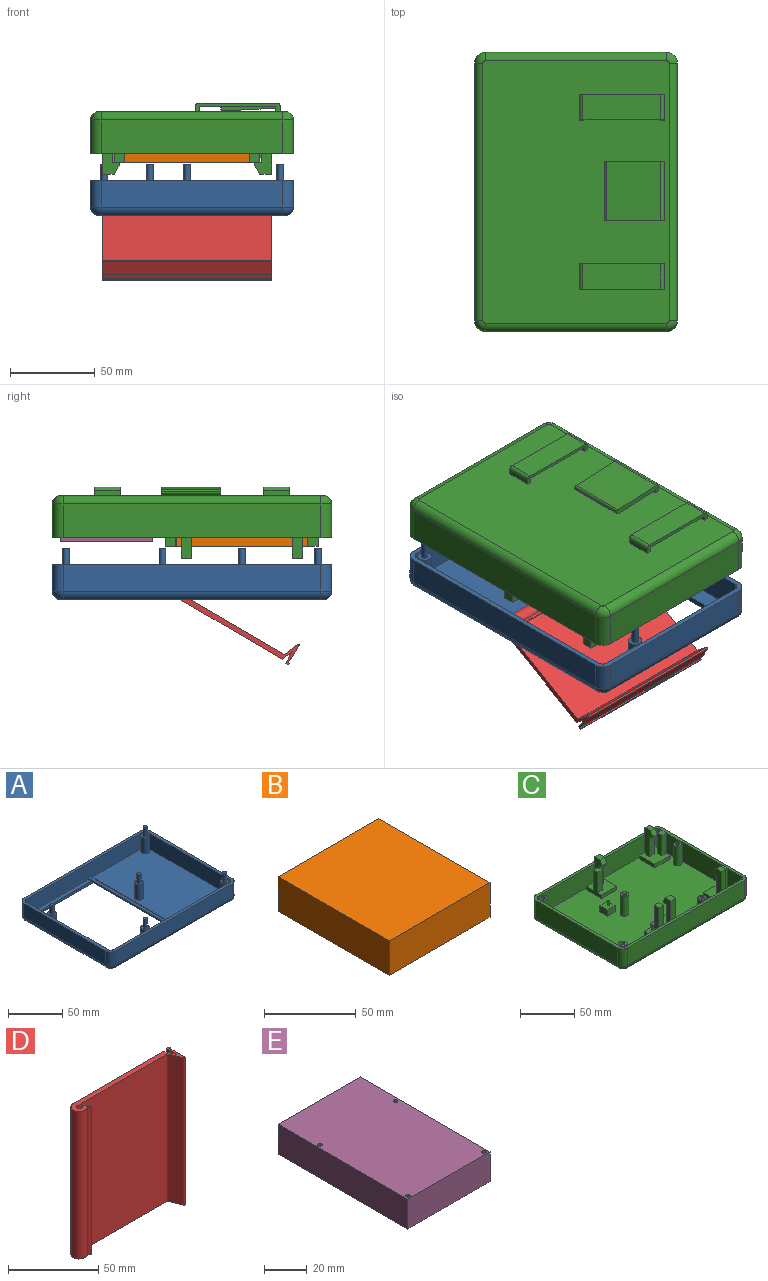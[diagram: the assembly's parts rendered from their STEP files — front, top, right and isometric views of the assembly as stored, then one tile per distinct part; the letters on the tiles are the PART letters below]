
ASSEMBLY  parts=5 mates=8
PART A: 52 faces, bbox 165x120x30.5 mm
  f0: plane 154.84x109.84mm, normal (0,0,-1), area 9006.2mm2, adj f19,f20,f21,f22,f23,f24,f25,f26
  f1: plane 159x114mm, normal (0,0,1), area 9865mm2, adj f11,f12,f13,f14,f15,f16,f17,f18
  f2: plane 107.3x15.92mm, normal (1,0,0), area 1708.2mm2, adj f3,f9,f10,f25
  f3: cylinder r=6.35mm len=15.92mm, axis (0,0,-1), area 158.8mm2, adj f2,f4,f10,f23
  f4: plane 152.3x15.92mm, normal (0,1,0), area 2424.6mm2, adj f3,f5,f10,f21
  f5: cylinder r=6.35mm len=15.92mm, axis (0,0,-1), area 158.8mm2, adj f4,f6,f10,f19
  f6: plane 107.3x15.92mm, normal (-1,0,0), area 1708.2mm2, adj f5,f7,f10,f20
  f7: cylinder r=6.35mm len=15.92mm, axis (0,0,-1), area 158.8mm2, adj f6,f8,f10,f22
  f8: plane 152.3x15.92mm, normal (0,-1,0), area 2424.6mm2, adj f7,f9,f10,f24
  f9: cylinder r=6.35mm len=15.92mm, axis (0,0,-1), area 158.8mm2, adj f2,f8,f10,f26
  f10: plane 165x120mm, normal (0,0,1), area 1649mm2, adj f2,f3,f4,f5,f6,f7,f8,f9
  f11: plane 107.3x18mm, normal (-1,0,0), area 1931.4mm2, adj f1,f10,f12,f18
  f12: cylinder r=3.35mm len=18mm, axis (0,0,-1), area 94.7mm2, adj f1,f10,f11,f13
  f13: plane 152.3x18mm, normal (0,-1,0), area 2734.3mm2, adj f1,f10,f12,f14,f51
  f14: cylinder r=3.35mm len=18mm, axis (0,0,-1), area 94.7mm2, adj f1,f10,f13,f15
  f15: plane 107.3x18mm, normal (1,0,0), area 1931.4mm2, adj f1,f10,f14,f16
  f16: cylinder r=3.35mm len=18mm, axis (0,0,-1), area 94.7mm2, adj f1,f10,f15,f17
  f17: plane 152.3x18mm, normal (0,1,0), area 2734.3mm2, adj f1,f10,f16,f18,f51
  f18: cylinder r=3.35mm len=18mm, axis (0,0,-1), area 94.7mm2, adj f1,f10,f11,f17
  f19: torus R=1.27mm, axis (0,0,1), area 56.5mm2, adj f0,f5,f20,f21
  f20: cylinder r=5.08mm len=107.3mm, axis (0,-1,0), area 856.2mm2, adj f0,f6,f19,f22
  f21: cylinder r=5.08mm len=152.3mm, axis (-1,0,0), area 1215.3mm2, adj f0,f4,f19,f23
  f22: torus R=1.27mm, axis (0,0,1), area 56.5mm2, adj f0,f7,f20,f24
  f23: torus R=1.27mm, axis (0,0,1), area 56.5mm2, adj f0,f3,f21,f25
  f24: cylinder r=5.08mm len=152.3mm, axis (1,0,0), area 1215.3mm2, adj f0,f8,f22,f26
  f25: cylinder r=5.08mm len=107.3mm, axis (0,1,0), area 856.2mm2, adj f0,f2,f23,f26
  f26: torus R=1.27mm, axis (0,0,1), area 56.5mm2, adj f0,f9,f24,f25
  f27: cylinder r=4mm len=17.5mm, axis (0,0,-1), area 439.8mm2, adj f1,f28
  f28: plane 8x8mm, normal (0,0,1), area 38.3mm2, adj f27,f37
  f29: cylinder r=4mm len=17.5mm, axis (0,0,-1), area 439.8mm2, adj f1,f30
  f30: plane 8x8mm, normal (0,0,1), area 38.3mm2, adj f29,f41
  f31: cylinder r=4mm len=17.5mm, axis (0,0,-1), area 439.8mm2, adj f1,f32
  f32: plane 8x8mm, normal (0,0,1), area 38.3mm2, adj f31,f39
  f33: cylinder r=4mm len=17.5mm, axis (0,0,-1), area 439.8mm2, adj f1,f34
  f34: plane 8x8mm, normal (0,0,1), area 38.3mm2, adj f33,f45
  f35: cylinder r=4mm len=17.5mm, axis (0,0,-1), area 439.8mm2, adj f1,f36
  f36: plane 8x8mm, normal (0,0,1), area 38.3mm2, adj f35,f43
  f37: cylinder r=1.95mm len=10mm, axis (0,0,-1), area 122.5mm2, adj f28,f38
  f38: plane 3.9x3.9mm, normal (0,0,1), area 11.9mm2, adj f37
  f39: cylinder r=1.95mm len=10mm, axis (0,0,-1), area 122.5mm2, adj f32,f40
  f40: plane 3.9x3.9mm, normal (0,0,1), area 11.9mm2, adj f39
  f41: cylinder r=1.95mm len=10mm, axis (0,0,-1), area 122.5mm2, adj f30,f42
  f42: plane 3.9x3.9mm, normal (0,0,1), area 11.9mm2, adj f41
  f43: cylinder r=1.95mm len=10mm, axis (0,0,-1), area 122.5mm2, adj f36,f44
  f44: plane 3.9x3.9mm, normal (0,0,1), area 11.9mm2, adj f43
  f45: cylinder r=1.95mm len=10mm, axis (0,0,-1), area 122.5mm2, adj f34,f46
  f46: plane 3.9x3.9mm, normal (0,0,1), area 11.9mm2, adj f45
  f47: plane 80x3mm, normal (0,1,0), area 240mm2, adj f0,f1,f48,f50
  f48: plane 100x3mm, normal (1,0,0), area 300mm2, adj f0,f1,f47,f49
  f49: plane 80x3mm, normal (0,-1,0), area 240mm2, adj f0,f1,f48,f50
  f50: plane 100x3mm, normal (-1,0,0), area 300mm2, adj f0,f1,f47,f49
  f51: cylinder r=1.5mm len=114mm, axis (0,1,0), area 1074.4mm2, adj f13,f17
PART B: 6 faces, bbox 77.6x85.4x23 mm
  f0: plane 85.4x23mm, normal (-1,0,0), area 1964.2mm2, adj f1,f3,f4,f5
  f1: plane 77.6x23mm, normal (0,-1,0), area 1784.8mm2, adj f0,f2,f4,f5
  f2: plane 85.4x23mm, normal (1,0,0), area 1964.2mm2, adj f1,f3,f4,f5
  f3: plane 77.6x23mm, normal (0,1,0), area 1784.8mm2, adj f0,f2,f4,f5
  f4: plane 85.4x77.6mm, normal (0,0,1), area 6627mm2, adj f0,f1,f2,f3
  f5: plane 85.4x77.6mm, normal (0,0,-1), area 6627mm2, adj f0,f1,f2,f3
PART C: 177 faces, bbox 165x120x42 mm
  f0: plane 155x110mm, normal (0,0,-1), area 16793.4mm2, adj f139,f140,f141,f142,f143,f144,f145,f146
  f1: plane 159x114mm, normal (0,0,1), area 15865mm2, adj f17,f18,f19,f20,f21,f22,f23,f24
  f2: plane 20x20mm, normal (0,0,1), area 340mm2, adj f33,f34,f35,f36,f52,f53,f54,f82
  f3: plane 6x4mm, normal (0,0,-1), area 24mm2, adj f74,f79,f80,f81
  f4: plane 6x4mm, normal (0,0,-1), area 24mm2, adj f66,f71,f72,f73
  f5: plane 20x20mm, normal (0,0,1), area 340mm2, adj f37,f38,f39,f40,f48,f49,f50,f66
  f6: plane 20x20mm, normal (0,0,1), area 340mm2, adj f29,f30,f31,f32,f45,f46,f47,f56
  f7: plane 20x20mm, normal (0,0,1), area 340mm2, adj f25,f26,f27,f28,f41,f42,f43,f74
  f8: plane 165x120mm, normal (0,0,1), area 1649mm2, adj f9,f10,f11,f12,f13,f14,f15,f16
  f9: plane 107.3x20mm, normal (-1,0,0), area 2146mm2, adj f8,f10,f16,f142
  f10: cylinder r=6.35mm len=20mm, axis (0,0,-1), area 199.5mm2, adj f8,f9,f11,f140
  f11: plane 152.3x20mm, normal (0,-1,0), area 3046mm2, adj f8,f10,f12,f139
  f12: cylinder r=6.35mm len=20mm, axis (0,0,-1), area 199.5mm2, adj f8,f11,f13,f141
  f13: plane 107.3x20mm, normal (1,0,0), area 2146mm2, adj f8,f12,f14,f143
  f14: cylinder r=6.35mm len=20mm, axis (0,0,-1), area 199.5mm2, adj f8,f13,f15,f145
  f15: plane 152.3x20mm, normal (0,1,0), area 3046mm2, adj f8,f14,f16,f146
  f16: cylinder r=6.35mm len=20mm, axis (0,0,-1), area 199.5mm2, adj f8,f9,f15,f144
  f17: plane 107.3x22mm, normal (1,0,0), area 2360.6mm2, adj f1,f8,f18,f24
  f18: cylinder r=3.35mm len=22mm, axis (0,0,-1), area 115.8mm2, adj f1,f8,f17,f19
  f19: plane 152.3x22mm, normal (0,1,0), area 3350.6mm2, adj f1,f8,f18,f20
  f20: cylinder r=3.35mm len=22mm, axis (0,0,-1), area 115.8mm2, adj f1,f8,f19,f21
  f21: plane 107.3x22mm, normal (-1,0,0), area 2360.6mm2, adj f1,f8,f20,f22
  f22: cylinder r=3.35mm len=22mm, axis (0,0,-1), area 115.8mm2, adj f1,f8,f21,f23
  f23: plane 152.3x22mm, normal (0,-1,0), area 3350.6mm2, adj f1,f8,f22,f24
  f24: cylinder r=3.35mm len=22mm, axis (0,0,-1), area 115.8mm2, adj f1,f8,f17,f23
  f25: plane 27x20mm, normal (1,0,0), area 218mm2, adj f1,f7,f26,f28,f41,f43,f44
  f26: plane 20x4mm, normal (0,1,0), area 80mm2, adj f1,f7,f25,f27
  f27: plane 20x4mm, normal (-1,0,0), area 80mm2, adj f1,f7,f26,f28
  f28: plane 20x4mm, normal (0,-1,0), area 80mm2, adj f1,f7,f25,f27
  f29: plane 20x4mm, normal (0,-1,0), area 80mm2, adj f1,f6,f30,f32
  f30: plane 20x4mm, normal (1,0,0), area 80mm2, adj f1,f6,f29,f31
  f31: plane 20x4mm, normal (0,1,0), area 80mm2, adj f1,f6,f30,f32
  f32: plane 27x20mm, normal (-1,0,0), area 218mm2, adj f1,f6,f29,f31,f45,f47,f65
  f33: plane 20x4mm, normal (0,-1,0), area 80mm2, adj f1,f2,f34,f36
  f34: plane 27x20mm, normal (1,0,0), area 218mm2, adj f1,f2,f33,f35,f52,f54,f55
  f35: plane 20x4mm, normal (0,1,0), area 80mm2, adj f1,f2,f34,f36
  f36: plane 20x4mm, normal (-1,0,0), area 80mm2, adj f1,f2,f33,f35
  f37: plane 27x20mm, normal (-1,0,0), area 218mm2, adj f1,f5,f38,f40,f48,f50,f51
  f38: plane 20x4mm, normal (0,-1,0), area 80mm2, adj f1,f5,f37,f39
  f39: plane 20x4mm, normal (1,0,0), area 80mm2, adj f1,f5,f38,f40
  f40: plane 20x4mm, normal (0,1,0), area 80mm2, adj f1,f5,f37,f39
  f41: plane 23x6mm, normal (0,1,0), area 138mm2, adj f7,f25,f42,f44
  f42: plane 23x6mm, normal (-1,0,0), area 138mm2, adj f7,f41,f43,f44
  f43: plane 23x6mm, normal (0,-1,0), area 138mm2, adj f7,f25,f42,f44
  f44: plane 6x6mm, normal (0,0,1), area 36mm2, adj f25,f41,f42,f43
  f45: plane 23x6mm, normal (0,-1,0), area 138mm2, adj f6,f32,f46,f65
  f46: plane 23x6mm, normal (1,0,0), area 138mm2, adj f6,f45,f47,f65
  f47: plane 23x6mm, normal (0,1,0), area 138mm2, adj f6,f32,f46,f65
  f48: plane 23x6mm, normal (0,-1,0), area 138mm2, adj f5,f37,f49,f51
  f49: plane 23x6mm, normal (1,0,0), area 138mm2, adj f5,f48,f50,f51
  f50: plane 23x6mm, normal (0,1,0), area 138mm2, adj f5,f37,f49,f51
  f51: plane 6x6mm, normal (0,0,1), area 36mm2, adj f37,f48,f49,f50
  f52: plane 23x6mm, normal (0,1,0), area 138mm2, adj f2,f34,f53,f55
  f53: plane 23x6mm, normal (-1,0,0), area 138mm2, adj f2,f52,f54,f55
  f54: plane 23x6mm, normal (0,-1,0), area 138mm2, adj f2,f34,f53,f55
  f55: plane 6x6mm, normal (0,0,1), area 36mm2, adj f34,f52,f53,f54
  f56: plane 6x3mm, normal (0,0.83,-0.55), area 21.6mm2, adj f6,f57,f63,f64
  f57: plane 27x6mm, normal (0,1,0), area 162mm2, adj f56,f58,f63,f64
  f58: plane 7x6mm, normal (0,0,1), area 42mm2, adj f57,f59,f63,f64
  f59: plane 6x5mm, normal (0,-0.86,0.51), area 35mm2, adj f58,f60,f63,f64
  f60: plane 6x2mm, normal (0,-1,0), area 12mm2, adj f59,f61,f63,f64
  f61: plane 6x4mm, normal (0,0,-1), area 24mm2, adj f60,f62,f63,f64
  f62: plane 23x6mm, normal (0,-1,0), area 138mm2, adj f6,f61,f63,f64
  f63: plane 30x10mm, normal (1,0,0), area 197.5mm2, adj f6,f56,f57,f58,f59,f60,f61,f62
  f64: plane 30x10mm, normal (-1,0,0), area 197.5mm2, adj f6,f56,f57,f58,f59,f60,f61,f62
  f65: plane 6x6mm, normal (0,0,1), area 36mm2, adj f32,f45,f46,f47
  f66: plane 23x6mm, normal (0,1,0), area 138mm2, adj f4,f5,f72,f73
  f67: plane 6x3mm, normal (0,-0.83,-0.55), area 21.6mm2, adj f5,f68,f72,f73
  f68: plane 27x6mm, normal (0,-1,0), area 162mm2, adj f67,f69,f72,f73
  f69: plane 7x6mm, normal (0,0,1), area 42mm2, adj f68,f70,f72,f73
  f70: plane 6x5mm, normal (0,0.86,0.51), area 35mm2, adj f69,f71,f72,f73
  f71: plane 6x2mm, normal (0,1,0), area 12mm2, adj f4,f70,f72,f73
  f72: plane 30x10mm, normal (1,0,0), area 197.5mm2, adj f4,f5,f66,f67,f68,f69,f70,f71
  f73: plane 30x10mm, normal (-1,0,0), area 197.5mm2, adj f4,f5,f66,f67,f68,f69,f70,f71
  f74: plane 23x6mm, normal (0,-1,0), area 138mm2, adj f3,f7,f80,f81
  f75: plane 6x3mm, normal (0,0.83,-0.55), area 21.6mm2, adj f7,f76,f80,f81
  f76: plane 27x6mm, normal (0,1,0), area 162mm2, adj f75,f77,f80,f81
  f77: plane 7x6mm, normal (0,0,1), area 42mm2, adj f76,f78,f80,f81
  f78: plane 6x5mm, normal (0,-0.86,0.51), area 35mm2, adj f77,f79,f80,f81
  f79: plane 6x2mm, normal (0,-1,0), area 12mm2, adj f3,f78,f80,f81
  f80: plane 30x10mm, normal (-1,0,0), area 197.5mm2, adj f3,f7,f74,f75,f76,f77,f78,f79
  f81: plane 30x10mm, normal (1,0,0), area 197.5mm2, adj f3,f7,f74,f75,f76,f77,f78,f79
  f82: plane 6x3mm, normal (0,-0.83,-0.55), area 21.6mm2, adj f2,f83,f89,f90
  f83: plane 27x6mm, normal (0,-1,0), area 162mm2, adj f82,f84,f89,f90
  f84: plane 7x6mm, normal (0,0,1), area 42mm2, adj f83,f85,f89,f90
  f85: plane 6x5mm, normal (0,0.86,0.51), area 35mm2, adj f84,f86,f89,f90
  f86: plane 6x2mm, normal (0,1,0), area 12mm2, adj f85,f87,f89,f90
  f87: plane 6x4mm, normal (0,0,-1), area 24mm2, adj f86,f88,f89,f90
  f88: plane 23x6mm, normal (0,1,0), area 138mm2, adj f2,f87,f89,f90
  f89: plane 30x10mm, normal (1,0,0), area 197.5mm2, adj f2,f82,f83,f84,f85,f86,f87,f88
  f90: plane 30x10mm, normal (-1,0,0), area 197.5mm2, adj f2,f82,f83,f84,f85,f86,f87,f88
  f91: cylinder r=4mm len=22mm, axis (0,0,1), area 552.9mm2, adj f1,f92
  f92: plane 8x8mm, normal (0,0,1), area 37.7mm2, adj f91,f108
  f93: cylinder r=4mm len=22mm, axis (0,0,1), area 552.9mm2, adj f1,f94
  f94: plane 8x8mm, normal (0,0,1), area 37.7mm2, adj f93,f110
  f95: cylinder r=4mm len=22mm, axis (0,0,1), area 552.9mm2, adj f1,f96
  f96: plane 8x8mm, normal (0,0,1), area 37.7mm2, adj f95,f102
  f97: cylinder r=4mm len=22mm, axis (0,0,1), area 552.9mm2, adj f1,f98
  f98: plane 8x8mm, normal (0,0,1), area 37.7mm2, adj f97,f104
  f99: cylinder r=4mm len=22mm, axis (0,0,1), area 552.9mm2, adj f1,f100
  f100: plane 8x8mm, normal (0,0,1), area 37.7mm2, adj f99,f106
  f101: cone r=0mm half-angle=59deg, axis (0,0,1), area 14.7mm2, adj f102
  f102: cylinder r=2mm len=10mm, axis (0,0,1), area 125.7mm2, adj f96,f101
  f103: cone r=0mm half-angle=59deg, axis (0,0,1), area 14.7mm2, adj f104
  f104: cylinder r=2mm len=10mm, axis (0,0,1), area 125.7mm2, adj f98,f103
  f105: cone r=0mm half-angle=59deg, axis (0,0,1), area 14.7mm2, adj f106
  f106: cylinder r=2mm len=10mm, axis (0,0,1), area 125.7mm2, adj f100,f105
  f107: cone r=0mm half-angle=59deg, axis (0,0,1), area 14.7mm2, adj f108
  f108: cylinder r=2mm len=10mm, axis (0,0,1), area 125.7mm2, adj f92,f107
  f109: cone r=0mm half-angle=59deg, axis (0,0,1), area 14.7mm2, adj f110
  f110: cylinder r=2mm len=10mm, axis (0,0,1), area 125.7mm2, adj f94,f109
  f111: plane 10x7mm, normal (0,1,0), area 70mm2, adj f1,f112,f114,f115
  f112: plane 10x7mm, normal (-1,0,0), area 70mm2, adj f1,f111,f113,f115
  f113: plane 10x7mm, normal (0,-1,0), area 70mm2, adj f1,f112,f114,f115
  f114: plane 10x7mm, normal (1,0,0), area 70mm2, adj f1,f111,f113,f115
  f115: plane 10x10mm, normal (0,0,1), area 97.2mm2, adj f111,f112,f113,f114,f131
  f116: plane 10x7mm, normal (1,0,0), area 70mm2, adj f1,f117,f119,f120
  f117: plane 10x7mm, normal (0,1,0), area 70mm2, adj f1,f116,f118,f120
  f118: plane 10x7mm, normal (-1,0,0), area 70mm2, adj f1,f117,f119,f120
  f119: plane 10x7mm, normal (0,-1,0), area 70mm2, adj f1,f116,f118,f120
  f120: plane 10x10mm, normal (0,0,1), area 97.2mm2, adj f116,f117,f118,f119,f137
  f121: plane 10x7mm, normal (-1,0,0), area 70mm2, adj f1,f122,f124,f125
  f122: plane 10x7mm, normal (0,-1,0), area 70mm2, adj f1,f121,f123,f125
  f123: plane 10x7mm, normal (1,0,0), area 70mm2, adj f1,f122,f124,f125
  f124: plane 10x7mm, normal (0,1,0), area 70mm2, adj f1,f121,f123,f125
  f125: plane 10x10mm, normal (0,0,1), area 97.2mm2, adj f121,f122,f123,f124,f133
  f126: plane 10x7mm, normal (0,-1,0), area 70mm2, adj f1,f127,f129,f130
  f127: plane 10x7mm, normal (1,0,0), area 70mm2, adj f1,f126,f128,f130
  f128: plane 10x7mm, normal (0,1,0), area 70mm2, adj f1,f127,f129,f130
  f129: plane 10x7mm, normal (-1,0,0), area 70mm2, adj f1,f126,f128,f130
  f130: plane 10x10mm, normal (0,0,1), area 97.2mm2, adj f126,f127,f128,f129,f135
  f131: cylinder r=0.95mm len=5mm, axis (0,0,-1), area 29.8mm2, adj f115,f132
  f132: plane 1.9x1.9mm, normal (0,0,1), area 2.8mm2, adj f131
  f133: cylinder r=0.95mm len=5mm, axis (0,0,-1), area 29.8mm2, adj f125,f134
  f134: plane 1.9x1.9mm, normal (0,0,1), area 2.8mm2, adj f133
  f135: cylinder r=0.95mm len=5mm, axis (0,0,-1), area 29.8mm2, adj f130,f136
  f136: plane 1.9x1.9mm, normal (0,0,1), area 2.8mm2, adj f135
  f137: cylinder r=0.95mm len=5mm, axis (0,0,-1), area 29.8mm2, adj f120,f138
  f138: plane 1.9x1.9mm, normal (0,0,1), area 2.8mm2, adj f137
  f139: cylinder r=5mm len=152.3mm, axis (1,0,0), area 1196.2mm2, adj f0,f11,f140,f141
  f140: torus R=1.35mm, axis (0,0,1), area 55.9mm2, adj f0,f10,f139,f142
  f141: torus R=1.35mm, axis (0,0,1), area 55.9mm2, adj f0,f12,f139,f143
  f142: cylinder r=5mm len=107.3mm, axis (0,-1,0), area 842.7mm2, adj f0,f9,f140,f144
  f143: cylinder r=5mm len=107.3mm, axis (0,1,0), area 842.7mm2, adj f0,f13,f141,f145
  f144: torus R=1.35mm, axis (0,0,1), area 55.9mm2, adj f0,f16,f142,f146
  f145: torus R=1.35mm, axis (0,0,1), area 55.9mm2, adj f0,f14,f143,f146
  f146: cylinder r=5mm len=152.3mm, axis (-1,0,0), area 1196.2mm2, adj f0,f15,f144,f145
  f147: plane 50x5mm, normal (-1,0,0), area 113.3mm2, adj f0,f148,f150,f151,f160,f161,f162,f165
  f148: plane 46x15mm, normal (0,0,-1), area 690mm2, adj f147,f149,f165,f166
  f149: plane 50x5mm, normal (1,0,0), area 113.3mm2, adj f0,f148,f150,f151,f160,f161,f162,f165
  f150: plane 15x3mm, normal (0,-1,0), area 45mm2, adj f0,f147,f149,f166
  f151: plane 15x3mm, normal (0,1,0), area 45mm2, adj f0,f147,f149,f165
  f152: plane 50x5mm, normal (1,0,0), area 113.3mm2, adj f0,f154,f155,f156,f157,f158,f159,f163
  f153: plane 50x5mm, normal (-1,0,0), area 113.3mm2, adj f0,f154,f155,f156,f157,f158,f159,f163
  f154: plane 46x15mm, normal (0,0,-1), area 690mm2, adj f152,f153,f163,f164
  f155: plane 15x3mm, normal (0,-1,0), area 45mm2, adj f0,f152,f153,f164
  f156: plane 15x3mm, normal (0,1,0), area 45mm2, adj f0,f152,f153,f163
  f157: plane 15x3mm, normal (0,1,0), area 45mm2, adj f0,f152,f153,f158
  f158: plane 45x15mm, normal (0,0,1), area 675mm2, adj f152,f153,f157,f159
  f159: plane 15x3mm, normal (0,-1,0), area 45mm2, adj f0,f152,f153,f158
  f160: plane 15x3mm, normal (0,-1,0), area 45mm2, adj f0,f147,f149,f161
  f161: plane 45x15mm, normal (0,0,1), area 675mm2, adj f147,f149,f160,f162
  f162: plane 15x3mm, normal (0,1,0), area 45mm2, adj f0,f147,f149,f161
  f163: cylinder r=2mm len=15mm, axis (1,0,0), area 47.1mm2, adj f152,f153,f154,f156
  f164: cylinder r=2mm len=15mm, axis (-1,0,0), area 47.1mm2, adj f152,f153,f154,f155
  f165: cylinder r=2mm len=15mm, axis (1,0,0), area 47.1mm2, adj f147,f148,f149,f151
  f166: cylinder r=2mm len=15mm, axis (-1,0,0), area 47.1mm2, adj f147,f148,f149,f150
  f167: plane 35x31.96mm, normal (0,0.05,-1), area 1120mm2, adj f168,f174,f175,f176
  f168: cylinder r=1mm len=35mm, axis (-1,0,0), area 53.2mm2, adj f167,f169,f175,f176
  f169: plane 35x1mm, normal (0,1,0), area 35mm2, adj f168,f170,f175,f176
  f170: cylinder r=1mm len=35mm, axis (-1,0,0), area 56.8mm2, adj f169,f171,f175,f176
  f171: plane 35x30.96mm, normal (0,-0.05,1), area 1085mm2, adj f170,f172,f175,f176
  f172: plane 35x1.95mm, normal (0,1,0), area 68.2mm2, adj f0,f171,f175,f176
  f173: plane 35x3mm, normal (0,-1,0), area 105mm2, adj f0,f174,f175,f176
  f174: cylinder r=2mm len=35mm, axis (-1,0,0), area 113.6mm2, adj f167,f173,f175,f176
  f175: plane 35.01x5mm, normal (1,0,0), area 109.8mm2, adj f0,f167,f168,f169,f170,f171,f172,f173
  f176: plane 35.01x5mm, normal (-1,0,0), area 109.8mm2, adj f0,f167,f168,f169,f170,f171,f172,f173
PART D: 20 faces, bbox 80.4x13.5x100 mm
  f0: plane 100x7.89mm, normal (-1,0,0), area 789.2mm2, adj f1,f17,f18,f19
  f1: plane 100x6.89mm, normal (0.93,0.38,0), area 743.9mm2, adj f0,f2,f18,f19
  f2: plane 100x71mm, normal (0,1,0), area 7100mm2, adj f1,f3,f18,f19
  f3: cylinder r=4.6mm len=100mm, axis (0,0,-1), area 1742.8mm2, adj f2,f4,f18,f19
  f4: plane 100x1.98mm, normal (-0.53,-0.85,0), area 233.9mm2, adj f3,f5,f18,f19
  f5: cylinder r=0.2mm len=100mm, axis (0,0,-1), area 54.5mm2, adj f4,f6,f18,f19
  f6: plane 100x4.59mm, normal (0.83,0.56,0), area 551.6mm2, adj f5,f7,f18,f19
  f7: cylinder r=0.2mm len=100mm, axis (0,0,-1), area 49.2mm2, adj f6,f8,f18,f19
  f8: cylinder r=1.6mm len=100mm, axis (0,0,-1), area 739.5mm2, adj f7,f9,f18,f19
  f9: plane 100x70.6mm, normal (0,-1,0), area 7060mm2, adj f8,f10,f18,f19
  f10: plane 100x9.2mm, normal (-0.93,-0.38,0), area 992.9mm2, adj f9,f11,f18,f19
  f11: cylinder r=0.5mm len=100mm, axis (0,0,-1), area 137.8mm2, adj f10,f12,f18,f19
  f12: plane 100x8.91mm, normal (1,0,0), area 891mm2, adj f11,f13,f18,f19
  f13: plane 100x0.3mm, normal (0,1,0), area 30mm2, adj f12,f14,f18,f19
  f14: plane 100x3.1mm, normal (1,0,0), area 310mm2, adj f13,f15,f18,f19
  f15: plane 100x0.8mm, normal (0,-1,0), area 80mm2, adj f14,f16,f18,f19
  f16: plane 100x1mm, normal (1,0,0), area 100mm2, adj f15,f17,f18,f19
  f17: plane 100x2mm, normal (0,1,0), area 200mm2, adj f0,f16,f18,f19
  f18: plane 80.4x13.51mm, normal (0,0,1), area 285.4mm2, adj f0,f1,f2,f3,f4,f5,f6,f7
  f19: plane 80.4x13.51mm, normal (0,0,-1), area 285.4mm2, adj f0,f1,f2,f3,f4,f5,f6,f7
PART E: 10 faces, bbox 54x85.6x17 mm
  f0: plane 85.6x17mm, normal (-1,0,0), area 1455.2mm2, adj f1,f3,f4,f5
  f1: plane 54x17mm, normal (0,-1,0), area 918mm2, adj f0,f2,f4,f5
  f2: plane 85.6x17mm, normal (1,0,0), area 1455.2mm2, adj f1,f3,f4,f5
  f3: plane 54x17mm, normal (0,1,0), area 918mm2, adj f0,f2,f4,f5
  f4: plane 85.6x54mm, normal (0,0,1), area 4609.8mm2, adj f0,f1,f2,f3,f6,f7,f8,f9
  f5: plane 85.6x54mm, normal (0,0,-1), area 4609.8mm2, adj f0,f1,f2,f3,f6,f7,f8,f9
  f6: cylinder r=1mm len=17mm, axis (0,0,1), area 106.8mm2, adj f4,f5
  f7: cylinder r=1mm len=17mm, axis (0,0,1), area 106.8mm2, adj f4,f5
  f8: cylinder r=1mm len=17mm, axis (0,0,1), area 106.8mm2, adj f4,f5
  f9: cylinder r=1mm len=17mm, axis (0,0,1), area 106.8mm2, adj f4,f5
PLACE A rot(axis=(0,0,1),90deg) t=(-50.42,-19.91,-25.51)mm
PLACE B rot(axis=(-0.71,-0.71,0),180deg) t=(-112.17,-18.28,29.04)mm
PLACE C rot(axis=(-0.71,0.71,0),180deg) t=(-63.05,-4.36,36.04)mm
PLACE D rot(axis=(-0.45,0.78,-0.45),104.3deg) t=(-118.17,-84.26,-42.98)mm
PLACE E rot(axis=(0,0,1),90deg) t=(-58.44,33.73,9.04)mm
MATE planar B.f4 <-> C.f61  axis (0,0,-1) through (-69.47,-50.44,6.04)mm
MATE planar E.f4 <-> C.f115  axis (0,0,1) through (-64,29.76,26.04)mm
MATE cylindrical A.f27 <-> C.f95  axis (0,0,-1) through (-13.17,53.76,-5.01)mm
MATE planar A.f49 <-> D.f19  axis (1,0,0) through (-118.17,-50.24,-24.01)mm
MATE planar B.f1 <-> C.f74  axis (-1,0,0) through (-112.17,-50.44,17.54)mm
MATE cylindrical A.f51 <-> D.f3  axis (-1,0,0) through (-65.17,-15.24,-20.96)mm
MATE planar C.f42 <-> B.f0  axis (0,1,0) through (-108.17,-89.24,17.54)mm
MATE cylindrical E.f6 <-> C.f131  axis (0,0,-1) through (-23.17,54.76,9.04)mm
